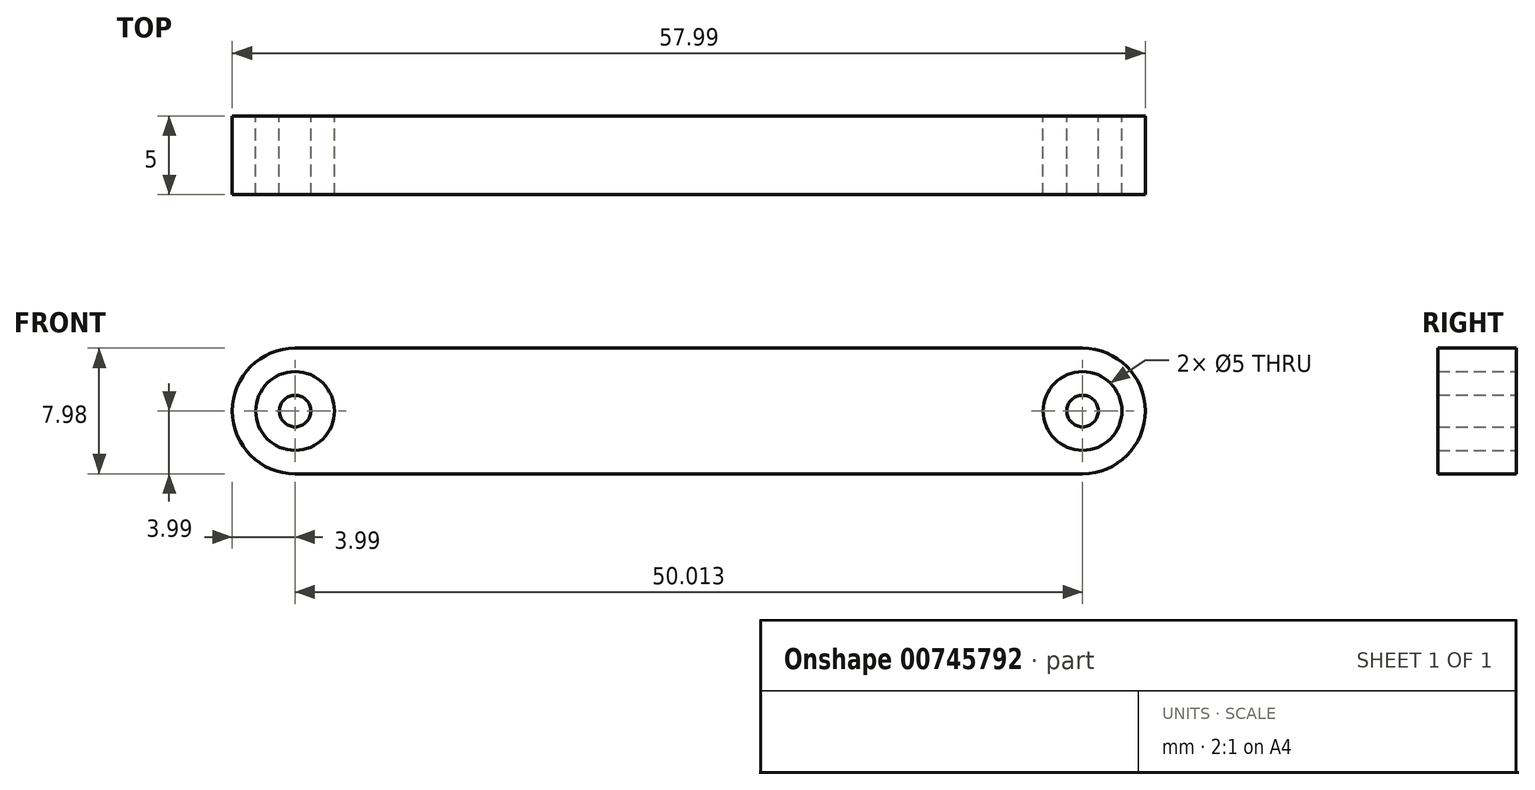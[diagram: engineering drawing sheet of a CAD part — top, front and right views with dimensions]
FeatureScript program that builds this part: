
annotation { "Feature Type Name" : "Feature", "Feature Type Description" : "" }
export const myFeature = defineFeature(function(context is Context, id is Id, definition is map)
    precondition{}
    {
        {
            var Q0;
            Q0=qCreatedBy(makeId("Front.planeOp"),FACE);
            var sketch = newSketch(context, id + "F0", { "sketchPlane" : qUnion([Q0])});
            skArc(sketch, "E0", {"start": v(0, 3.99) * mm, "mid": v(-3.99, 0) * mm, "end": v(0, -3.99) * mm});
            skCircle(sketch, "E1", {"center": v(0, 0) * mm, "radius": 2.5 * mm});
            skCircle(sketch, "E2", {"center": v(0, 0) * mm, "radius": 1 * mm});
            skArc(sketch, "E3", {"start": v(50.01, -3.99) * mm, "mid": v(54, 0) * mm, "end": v(50.01, 3.99) * mm});
            skCircle(sketch, "E4", {"center": v(50.01, 0) * mm, "radius": 2.5 * mm});
            skCircle(sketch, "E5", {"center": v(50.01, 0) * mm, "radius": 1 * mm});
            skLineSegment(sketch, "E6", {"start": v(0, 3.99) * mm, "end": v(50.01, 3.99) * mm});
            skLineSegment(sketch, "E7", {"start": v(0, -3.99) * mm, "end": v(50.01, -3.99) * mm});
            skSolve(sketch);
        }
        {
            var Q0;
            Q0 = qSketchRegion(id + "F0", true);
            var Q1;
            Q1=makeQuery(id+"F0.imprint","IMPRINT",FACE,{"disambiguationData":[TD([[makeQuery(id+"F0.imprint","IMPRINT",EDGE,{"derivedFrom":sQuery(id+"F0.wireOp",EDGE,"E2")}),1.0]])]});
            var Q2;
            Q2=makeQuery(id+"F0.imprint","IMPRINT",FACE,{"disambiguationData":[TD([[makeQuery(id+"F0.imprint","IMPRINT",EDGE,{"derivedFrom":sQuery(id+"F0.wireOp",EDGE,"E5")}),1.0]])]});
            extrude(context, id + "F1", {"entities" : qUnion([Q0, Q1, Q2]), "depth" : 5 * mm, "offsetDistance" : 25.4 * mm});
        }
    });
